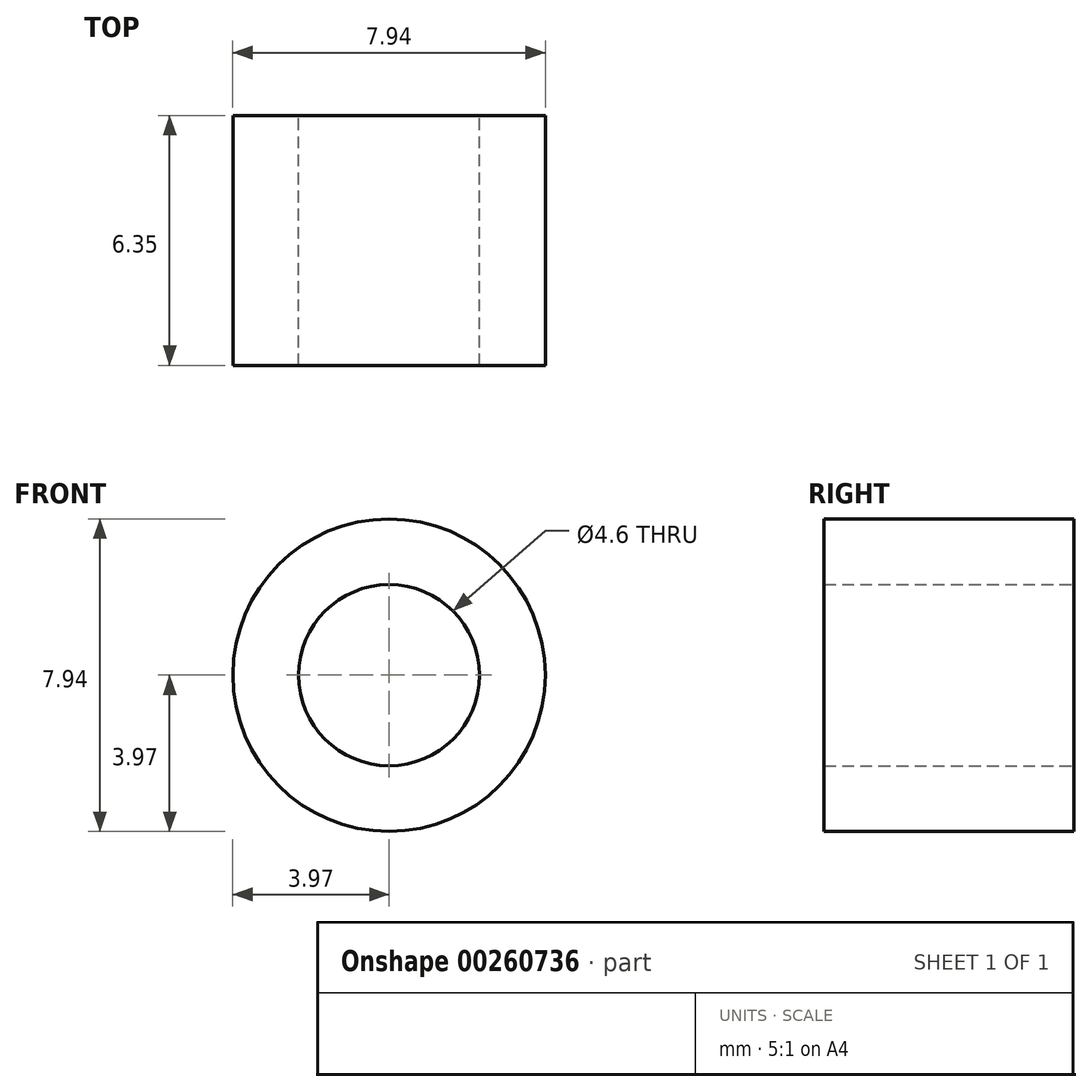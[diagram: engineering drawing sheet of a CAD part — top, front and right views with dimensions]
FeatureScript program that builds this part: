
annotation { "Feature Type Name" : "Feature", "Feature Type Description" : "" }
export const myFeature = defineFeature(function(context is Context, id is Id, definition is map)
    precondition{}
    {
        {
            var Q0;
            Q0=qCreatedBy(makeId("Front.planeOp"),FACE);
            var sketch = newSketch(context, id + "F0", { "sketchPlane" : qUnion([Q0])});
            skCircle(sketch, "E0", {"center": v(0, 0) * mm, "radius": 3.97 * mm});
            skCircle(sketch, "E1", {"center": v(0, 0) * mm, "radius": 2.3 * mm});
            skSolve(sketch);
        }
        {
            var Q0;
            Q0=makeQuery(id+"F0.imprint","IMPRINT",FACE,{"disambiguationData":[TD([[makeQuery(id+"F0.imprint","IMPRINT",EDGE,{"derivedFrom":sQuery(id+"F0.wireOp",EDGE,"E0")}),1.0]])]});
            extrude(context, id + "F1", {"entities" : qUnion([Q0]), "depth" : 6.35 * mm});
        }
    });
